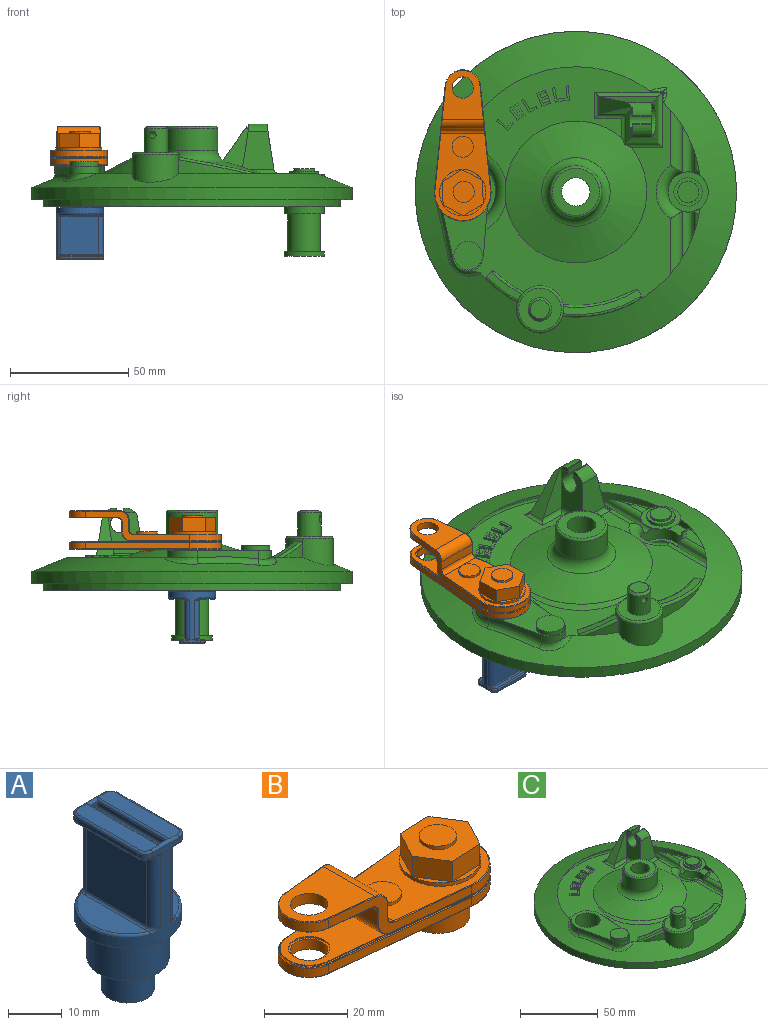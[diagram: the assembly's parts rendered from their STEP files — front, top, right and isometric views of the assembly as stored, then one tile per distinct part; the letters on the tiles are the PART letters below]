
ASSEMBLY  parts=3 mates=2
PART A: 97 faces, bbox 21.6x22x38 mm
  f0: plane 19x3.5mm, normal (0,0,1), area 65.5mm2, adj f39,f40,f42,f59,f60,f61
  f1: plane 19x3.5mm, normal (0,0,1), area 65.5mm2, adj f39,f41,f42,f56,f57,f58
  f2: cylinder r=10mm len=20mm, axis (0,0,-1), area 247.8mm2, adj f5,f23,f24,f25,f26,f27,f28,f30
  f3: plane 16x15.87mm, normal (1,0,0), area 254mm2, adj f25,f26,f31,f76
  f4: plane 16x15.87mm, normal (-1,0,0), area 254mm2, adj f23,f24,f37,f87
  f5: plane 20x20mm, normal (0,0,-1), area 127.9mm2, adj f2,f93
  f6: plane 17.81x6.2mm, normal (0,0,1), area 76.9mm2, adj f34,f35,f37,f38
  f7: plane 17.81x6.2mm, normal (0,0,1), area 76.9mm2, adj f28,f29,f31,f32
  f8: plane 7x1.5mm, normal (0,1,0), area 8.1mm2, adj f19,f22,f39,f47,f49,f51,f67,f69
  f9: plane 16x1mm, normal (-1,0,0), area 16mm2, adj f19,f20,f60,f66
  f10: plane 7x1.5mm, normal (0,-1,0), area 8.1mm2, adj f20,f21,f42,f48,f50,f52,f62,f63
  f11: plane 19x2.05mm, normal (0,0,-1), area 28.1mm2, adj f64,f65,f66,f68,f70,f86,f87,f88
  f12: plane 16x1mm, normal (1,0,0), area 16mm2, adj f21,f22,f55,f57
  f13: plane 19x2.05mm, normal (0,0,-1), area 28.1mm2, adj f51,f52,f53,f54,f55,f75,f76,f77
  f14: plane 2x1mm, normal (0,-1,0), area 2mm2, adj f15,f17,f39,f43
  f15: plane 18x1mm, normal (1,0,0), area 18mm2, adj f14,f16,f40,f44
  f16: plane 2x1mm, normal (0,1,0), area 2mm2, adj f15,f17,f42,f46
  f17: plane 18x1mm, normal (-1,0,0), area 18mm2, adj f14,f16,f41,f45
  f18: plane 17x1mm, normal (0,0,1), area 17mm2, adj f43,f44,f45,f46
  f19: cylinder r=2mm len=2mm, axis (0,0,-1), area 3.1mm2, adj f8,f9,f61,f68
  f20: cylinder r=2mm len=2mm, axis (0,0,1), area 3.1mm2, adj f9,f10,f59,f65
  f21: cylinder r=2mm len=2mm, axis (0,0,-1), area 3.1mm2, adj f10,f12,f54,f56
  f22: cylinder r=2mm len=2mm, axis (0,0,1), area 3.1mm2, adj f8,f12,f53,f58
  f23: cylinder r=2mm len=16.38mm, axis (0,0,-1), area 46.6mm2, adj f2,f4,f35,f88,f89,f90
  f24: cylinder r=2mm len=16.38mm, axis (0,0,-1), area 46.6mm2, adj f2,f4,f38,f84,f85,f86
  f25: cylinder r=2mm len=16.38mm, axis (0,0,-1), area 46.6mm2, adj f2,f3,f29,f73,f74,f75
  f26: cylinder r=2mm len=16.38mm, axis (0,0,-1), area 46.6mm2, adj f2,f3,f32,f77,f78,f79
  f27: bspline ~2.56x1.18mm, area 0.6mm2, adj f2,f28,f29
  f28: torus R=9.5mm, axis (0,0,1), area 18.7mm2, adj f2,f7,f27,f30
  f29: torus R=2.5mm, axis (0,0,1), area 1.5mm2, adj f7,f25,f27,f31
  f30: bspline ~2.56x1.18mm, area 0.6mm2, adj f2,f28,f32
  f31: cylinder r=0.5mm len=15.87mm, axis (0,1,0), area 12.5mm2, adj f3,f7,f29,f32
  f32: torus R=2.5mm, axis (0,0,1), area 1.5mm2, adj f7,f26,f30,f31
  f33: bspline ~2.56x1.18mm, area 0.6mm2, adj f2,f34,f35
  f34: torus R=9.5mm, axis (0,0,1), area 18.7mm2, adj f2,f6,f33,f36
  f35: torus R=2.5mm, axis (0,0,1), area 1.5mm2, adj f6,f23,f33,f37
  f36: bspline ~2.56x1.18mm, area 0.6mm2, adj f2,f34,f38
  f37: cylinder r=0.5mm len=15.87mm, axis (0,-1,0), area 12.5mm2, adj f4,f6,f35,f38
  f38: torus R=2.5mm, axis (0,0,1), area 1.5mm2, adj f6,f24,f36,f37
  f39: cylinder r=0.5mm len=7mm, axis (1,0,0), area 7.5mm2, adj f0,f1,f8,f14,f40,f41,f58,f61
  f40: cylinder r=0.5mm len=19mm, axis (0,1,0), area 14.5mm2, adj f0,f15,f39,f42
  f41: cylinder r=0.5mm len=19mm, axis (0,-1,0), area 14.5mm2, adj f1,f17,f39,f42
  f42: cylinder r=0.5mm len=7mm, axis (-1,0,0), area 7.5mm2, adj f0,f1,f10,f16,f40,f41,f56,f59
  f43: cylinder r=0.5mm len=2mm, axis (-1,0,0), area 1.2mm2, adj f14,f18,f44,f45
  f44: cylinder r=0.5mm len=18mm, axis (0,-1,0), area 13.7mm2, adj f15,f18,f43,f46
  f45: cylinder r=0.5mm len=18mm, axis (0,1,0), area 13.7mm2, adj f17,f18,f43,f46
  f46: cylinder r=0.5mm len=2mm, axis (1,0,0), area 1.2mm2, adj f16,f18,f44,f45
  f47: bspline ~1.52x0.32mm, area 0.1mm2, adj f8,f49,f81
  f48: bspline ~1.52x0.32mm, area 0.1mm2, adj f10,f50,f71
  f49: bspline ~1.38x0.57mm, area 0.3mm2, adj f8,f47,f51,f79,f80
  f50: bspline ~1.38x0.57mm, area 0.3mm2, adj f10,f48,f52,f72,f73
  f51: cylinder r=0.5mm len=1.25mm, axis (1,0,0), area 0.9mm2, adj f8,f13,f49,f53,f78
  f52: cylinder r=0.5mm len=1.25mm, axis (-1,0,0), area 0.9mm2, adj f10,f13,f50,f54,f74
  f53: torus R=1.5mm, axis (0,0,1), area 2.2mm2, adj f13,f22,f51,f55
  f54: torus R=1.5mm, axis (0,0,1), area 2.2mm2, adj f13,f21,f52,f55
  f55: cylinder r=0.5mm len=16mm, axis (0,-1,0), area 12.6mm2, adj f12,f13,f53,f54
  f56: torus R=1.5mm, axis (0,0,1), area 2.2mm2, adj f1,f21,f42,f57
  f57: cylinder r=0.5mm len=16mm, axis (0,1,0), area 12.6mm2, adj f1,f12,f56,f58
  f58: torus R=1.5mm, axis (0,0,1), area 2.2mm2, adj f1,f22,f39,f57
  f59: torus R=1.5mm, axis (0,0,1), area 2.2mm2, adj f0,f20,f42,f60
  f60: cylinder r=0.5mm len=16mm, axis (0,-1,0), area 12.6mm2, adj f0,f9,f59,f61
  f61: torus R=1.5mm, axis (0,0,1), area 2.2mm2, adj f0,f19,f39,f60
  f62: bspline ~1.52x0.32mm, area 0.1mm2, adj f10,f63,f82
  f63: bspline ~1.38x0.57mm, area 0.3mm2, adj f10,f62,f64,f83,f84
  f64: cylinder r=0.5mm len=1.25mm, axis (-1,0,0), area 0.9mm2, adj f10,f11,f63,f65,f85
  f65: torus R=1.5mm, axis (0,0,1), area 2.2mm2, adj f11,f20,f64,f66
  f66: cylinder r=0.5mm len=16mm, axis (0,1,0), area 12.6mm2, adj f9,f11,f65,f68
  f67: bspline ~1.52x0.32mm, area 0.1mm2, adj f8,f69,f92
  f68: torus R=1.5mm, axis (0,0,1), area 2.2mm2, adj f11,f19,f66,f70
  f69: bspline ~1.38x0.57mm, area 0.3mm2, adj f8,f67,f70,f90,f91
  f70: cylinder r=0.5mm len=1.25mm, axis (1,0,0), area 0.9mm2, adj f8,f11,f68,f69,f89
  f71: bspline ~1.6x0.24mm, area 0.1mm2, adj f2,f48,f72
  f72: bspline ~0.49x0.24mm, area 0mm2, adj f2,f50,f71,f73
  f73: bspline ~1.27x0.43mm, area 0.3mm2, adj f25,f50,f72,f74
  f74: bspline ~1.32x0.85mm, area 0.5mm2, adj f25,f52,f73,f75
  f75: torus R=2.5mm, axis (0,0,1), area 1.2mm2, adj f13,f25,f74,f76
  f76: cylinder r=0.5mm len=15.87mm, axis (0,-1,0), area 12.5mm2, adj f3,f13,f75,f77
  f77: torus R=2.5mm, axis (0,0,1), area 1.2mm2, adj f13,f26,f76,f78
  f78: bspline ~1.32x0.85mm, area 0.5mm2, adj f26,f51,f77,f79
  f79: bspline ~1.27x0.43mm, area 0.3mm2, adj f26,f49,f78,f80
  f80: bspline ~0.5x0.24mm, area 0mm2, adj f2,f49,f79,f81
  f81: bspline ~1.93x0.29mm, area 0.1mm2, adj f2,f47,f80
  f82: bspline ~1.93x0.29mm, area 0.1mm2, adj f2,f62,f83
  f83: bspline ~0.5x0.24mm, area 0mm2, adj f2,f63,f82,f84
  f84: bspline ~1.27x0.43mm, area 0.3mm2, adj f24,f63,f83,f85
  f85: bspline ~1.32x0.85mm, area 0.5mm2, adj f24,f64,f84,f86
  f86: torus R=2.5mm, axis (0,0,1), area 1.2mm2, adj f11,f24,f85,f87
  f87: cylinder r=0.5mm len=15.87mm, axis (0,1,0), area 12.5mm2, adj f4,f11,f86,f88
  f88: torus R=2.5mm, axis (0,0,1), area 1.2mm2, adj f11,f23,f87,f89
  f89: bspline ~1.32x0.85mm, area 0.5mm2, adj f23,f70,f88,f90
  f90: bspline ~1.27x0.43mm, area 0.3mm2, adj f23,f69,f89,f91
  f91: bspline ~0.49x0.24mm, area 0mm2, adj f2,f69,f90,f92
  f92: bspline ~1.6x0.24mm, area 0.1mm2, adj f2,f67,f91
  f93: cylinder r=7.7mm len=15.4mm, axis (0,0,1), area 435.4mm2, adj f5,f94
  f94: plane 15.4x15.4mm, normal (0,0,-1), area 107.7mm2, adj f93,f95
  f95: cylinder r=5mm len=10mm, axis (0,0,1), area 219.9mm2, adj f94,f96
  f96: plane 10x10mm, normal (0,0,-1), area 78.5mm2, adj f95
PART B: 91 faces, bbox 65.6x26x25.4 mm
  f0: plane 36.8x23.6mm, normal (0,0,1), area 381.9mm2, adj f28,f55,f56,f57,f67,f69
  f1: plane 17.66x4.03mm, normal (-1,0,0), area 71.1mm2, adj f25,f27,f48,f49
  f2: plane 18.28x0.31mm, normal (-1,0,0), area 1.8mm2, adj f12,f14,f15,f16,f25,f29,f32,f42
  f3: plane 10x10mm, normal (0,0,1), area 14.9mm2, adj f7,f13
  f4: cylinder r=7.5mm len=14.92mm, axis (0,0,-1), area 57.3mm2, adj f5,f8,f34,f38
  f5: plane 44.05x4.48mm, normal (-0.1,-0.99,0), area 115.1mm2, adj f4,f6,f33,f37
  f6: cylinder r=12mm len=24mm, axis (0,0,-1), area 104.3mm2, adj f5,f8,f35,f39
  f7: cylinder r=4.5mm len=9mm, axis (0,0,-1), area 84.8mm2, adj f3,f10
  f8: plane 44.05x4.48mm, normal (-0.1,0.99,0), area 115.1mm2, adj f4,f6,f36,f40
  f9: plane 63.6x23.6mm, normal (0,0,1), area 14.9mm2, adj f29,f30,f31,f32,f37,f38,f39,f40
  f10: plane 63.6x23.6mm, normal (0,0,-1), area 875.7mm2, adj f7,f33,f34,f35,f36,f86,f87
  f11: cylinder r=7mm len=13.93mm, axis (0,0,-1), area 4.1mm2, adj f12,f14,f15,f30
  f12: plane 18.21x1.85mm, normal (-0.1,-0.99,0), area 3.7mm2, adj f2,f11,f15,f29
  f13: cylinder r=5mm len=10mm, axis (0,0,-1), area 12.6mm2, adj f3,f15
  f14: plane 18.21x1.85mm, normal (-0.1,0.99,0), area 3.7mm2, adj f2,f11,f15,f32
  f15: plane 24.5x17.63mm, normal (0,0,1), area 275.8mm2, adj f2,f11,f12,f13,f14
  f16: plane 38.8x23.6mm, normal (0,0,-1), area 9.1mm2, adj f2,f29,f31,f32,f41,f42,f43
  f17: plane 44.05x12.6mm, normal (-0.1,0.99,0), area 137.2mm2, adj f19,f22,f42,f44,f46,f48,f50,f52
  f18: plane 44.05x12.6mm, normal (-0.1,-0.99,0), area 137.2mm2, adj f19,f22,f43,f45,f47,f49,f51,f53
  f19: cylinder r=12mm len=24mm, axis (0,0,-1), area 104.3mm2, adj f17,f18,f41,f55
  f20: plane 18.19x4mm, normal (1,0,0), area 72.8mm2, adj f26,f28,f60,f61
  f21: plane 20.8x17.42mm, normal (0,0,1), area 236.7mm2, adj f23,f26,f64,f65,f66
  f22: cylinder r=7.5mm len=14.92mm, axis (0,0,1), area 57.3mm2, adj f17,f18,f54,f66
  f23: cylinder r=4.5mm len=9mm, axis (0,0,1), area 84.8mm2, adj f21,f24
  f24: plane 19.8x17.22mm, normal (0,0,-1), area 219.4mm2, adj f23,f27,f52,f53,f54
  f25: cylinder r=4mm len=18.24mm, axis (0,1,0), area 94.7mm2, adj f1,f2,f46,f47
  f26: cylinder r=4mm len=18.19mm, axis (0,-1,0), area 111.9mm2, adj f20,f21,f62,f63
  f27: cylinder r=2mm len=17.66mm, axis (0,1,0), area 54.8mm2, adj f1,f24,f50,f51
  f28: cylinder r=2mm len=18.64mm, axis (0,1,0), area 57.9mm2, adj f0,f20,f58,f59
  f29: cylinder r=0.2mm len=44.07mm, axis (0.99,-0.1,0), area 22.1mm2, adj f2,f9,f12,f16,f30,f31
  f30: torus R=7.2mm, axis (0,0,1), area 6.5mm2, adj f9,f11,f29,f32
  f31: torus R=11.7mm, axis (0,0,1), area 24.3mm2, adj f9,f16,f29,f32
  f32: cylinder r=0.2mm len=44.07mm, axis (-0.99,-0.1,0), area 22.1mm2, adj f2,f9,f14,f16,f30,f31
  f33: cylinder r=0.2mm len=44.07mm, axis (0.99,-0.1,0), area 13.9mm2, adj f5,f10,f34,f35
  f34: torus R=7.3mm, axis (0,0,1), area 6.9mm2, adj f4,f10,f33,f36
  f35: torus R=11.8mm, axis (0,0,1), area 12.5mm2, adj f6,f10,f33,f36
  f36: cylinder r=0.2mm len=44.07mm, axis (-0.99,-0.1,0), area 13.9mm2, adj f8,f10,f34,f35
  f37: cylinder r=0.2mm len=44.07mm, axis (-0.99,0.1,0), area 13.9mm2, adj f5,f9,f38,f39
  f38: torus R=7.3mm, axis (0,0,1), area 6.9mm2, adj f4,f9,f37,f40
  f39: torus R=11.8mm, axis (0,0,1), area 12.5mm2, adj f6,f9,f37,f40
  f40: cylinder r=0.2mm len=44.07mm, axis (0.99,0.1,0), area 13.9mm2, adj f8,f9,f38,f39
  f41: torus R=11.8mm, axis (0,0,1), area 12.5mm2, adj f16,f19,f42,f43
  f42: cylinder r=0.2mm len=25.83mm, axis (-0.99,-0.1,0), area 8.1mm2, adj f2,f16,f17,f41,f44
  f43: cylinder r=0.2mm len=25.83mm, axis (0.99,-0.1,0), area 8.1mm2, adj f2,f16,f18,f41,f45
  f44: cylinder r=0.2mm len=0.26mm, axis (0,0,1), area 0mm2, adj f2,f17,f42,f46
  f45: cylinder r=0.2mm len=0.26mm, axis (0,0,1), area 0mm2, adj f2,f18,f43,f47
  f46: bspline ~3.91x3.18mm, area 1.6mm2, adj f2,f17,f25,f44,f48
  f47: bspline ~3.91x3.18mm, area 1.6mm2, adj f2,f18,f25,f45,f49
  f48: cylinder r=0.2mm len=4.03mm, axis (0,0,1), area 1.2mm2, adj f1,f17,f46,f50
  f49: cylinder r=0.2mm len=4.03mm, axis (0,0,1), area 1.2mm2, adj f1,f18,f47,f51
  f50: bspline ~2.58x2.2mm, area 1mm2, adj f17,f27,f48,f52
  f51: bspline ~2.58x2.58mm, area 1mm2, adj f18,f27,f49,f53
  f52: cylinder r=0.2mm len=13.26mm, axis (-0.99,-0.1,0), area 4.2mm2, adj f17,f24,f50,f54
  f53: cylinder r=0.2mm len=13.26mm, axis (-0.99,0.1,0), area 4.2mm2, adj f18,f24,f51,f54
  f54: torus R=7.3mm, axis (0,0,1), area 6.9mm2, adj f22,f24,f52,f53
  f55: torus R=11.8mm, axis (0,0,1), area 12.5mm2, adj f0,f19,f56,f57
  f56: cylinder r=0.2mm len=23.83mm, axis (0.99,0.1,0), area 7.5mm2, adj f0,f17,f55,f58
  f57: cylinder r=0.2mm len=23.83mm, axis (-0.99,0.1,0), area 7.5mm2, adj f0,f18,f55,f59
  f58: bspline ~2.22x2.2mm, area 1.1mm2, adj f17,f28,f56,f60
  f59: bspline ~2.22x2.2mm, area 1.1mm2, adj f18,f28,f57,f61
  f60: cylinder r=0.2mm len=4mm, axis (0,0,-1), area 1.3mm2, adj f17,f20,f58,f62
  f61: cylinder r=0.2mm len=4mm, axis (0,0,-1), area 1.3mm2, adj f18,f20,f59,f63
  f62: bspline ~4.02x4mm, area 2mm2, adj f17,f26,f60,f64
  f63: bspline ~4.02x4mm, area 2mm2, adj f18,f26,f61,f65
  f64: cylinder r=0.2mm len=14.26mm, axis (0.99,0.1,0), area 4.5mm2, adj f17,f21,f62,f66
  f65: cylinder r=0.2mm len=14.26mm, axis (0.99,-0.1,0), area 4.5mm2, adj f18,f21,f63,f66
  f66: torus R=7.3mm, axis (0,0,1), area 6.9mm2, adj f21,f22,f64,f65
  f67: cylinder r=4.5mm len=9mm, axis (0,0,-1), area 28.3mm2, adj f0,f68
  f68: plane 9x9mm, normal (0,0,1), area 63.6mm2, adj f67
  f69: cylinder r=9.81mm len=19.63mm, axis (0,0,-1), area 61.7mm2, adj f0,f70,f71,f72,f73,f74,f75
  f70: plane 8.3x5.24mm, normal (0,0,1), area 8.7mm2, adj f69,f82
  f71: plane 9.81x1.52mm, normal (0,0,1), area 8.7mm2, adj f69,f81
  f72: plane 8.69x4.57mm, normal (0,0,1), area 8.7mm2, adj f69,f80
  f73: plane 8.3x5.24mm, normal (0,0,1), area 8.7mm2, adj f69,f79
  f74: plane 9.81x1.52mm, normal (0,0,1), area 8.7mm2, adj f69,f78
  f75: plane 8.69x4.57mm, normal (0,0,1), area 8.7mm2, adj f69,f77
  f76: plane 19.61x17.38mm, normal (0,0,1), area 186.7mm2, adj f77,f78,f79,f80,f81,f82,f83
  f77: plane 8.69x6mm, normal (-0.89,0.46,0), area 58.9mm2, adj f75,f76,f78,f82
  f78: plane 9.81x6mm, normal (-0.04,1,0), area 58.9mm2, adj f74,f76,f77,f79
  f79: plane 8.3x6mm, normal (0.85,0.53,0), area 58.9mm2, adj f73,f76,f78,f80
  f80: plane 8.69x6mm, normal (0.89,-0.46,0), area 58.9mm2, adj f72,f76,f79,f81
  f81: plane 9.81x6mm, normal (0.04,-1,0), area 58.9mm2, adj f71,f76,f80,f82
  f82: plane 8.3x6mm, normal (-0.85,-0.53,0), area 58.9mm2, adj f70,f76,f77,f81
  f83: cylinder r=4.5mm len=9mm, axis (0,0,-1), area 28.3mm2, adj f76,f84
  f84: plane 9x9mm, normal (0,0,1), area 63.6mm2, adj f83
  f85: plane 0.3x0.3mm, normal (0,0,-1), area 0.1mm2, adj f86
  f86: torus R=0.15mm, axis (0,0,1), area 34.4mm2, adj f10,f85
  f87: cylinder r=7.7mm len=15.4mm, axis (0,0,1), area 435.4mm2, adj f10,f88
  f88: plane 15.4x15.4mm, normal (0,0,-1), area 99.7mm2, adj f87,f89
  f89: cylinder r=5.25mm len=10.5mm, axis (0,0,-1), area 263.9mm2, adj f88,f90
  f90: plane 10.5x10.5mm, normal (0,0,-1), area 86.6mm2, adj f89
PART C: 208 faces, bbox 138.4x138.4x58.4 mm
  f0: plane 112.54x103.07mm, normal (0,0,1), area 4306.9mm2, adj f3,f93,f94,f95,f99,f101,f103,f111
  f1: plane 3.88x2mm, normal (-1,0,0), area 6.6mm2, adj f5,f130,f133,f135,f142
  f2: plane 4.97x2mm, normal (1,0,0), area 3.1mm2, adj f131,f134,f136,f137,f140
  f3: cone r=53mm half-angle=68.2deg, axis (0,0,-1), area 5588.4mm2, adj f0,f21,f99,f100,f101,f102,f103,f113
  f4: cylinder r=4mm len=8.03mm, axis (1,0,0), area 177mm2, adj f135,f136,f138,f142
  f5: plane 8x0.5mm, normal (0,0,1), area 4mm2, adj f1,f7,f133,f135
  f6: plane 4.97x2mm, normal (-1,0,0), area 7.2mm2, adj f131,f134,f136,f142
  f7: plane 4.97x2mm, normal (1,0,0), area 3.1mm2, adj f5,f133,f135,f137,f140
  f8: cylinder r=3mm len=6mm, axis (0,0,-1), area 30.3mm2, adj f9,f10,f11,f63,f82,f83,f84,f85
  f9: plane 1.69x1.69mm, normal (0,0,-1), area 1.8mm2, adj f8,f85,f91
  f10: plane 1.69x1.69mm, normal (0,0,-1), area 1.8mm2, adj f8,f88,f89
  f11: plane 1.69x1.69mm, normal (0,0,-1), area 1.8mm2, adj f8,f86,f87
  f12: cylinder r=61mm len=122mm, axis (0,0,-1), area 1352mm2, adj f17,f33,f38,f39,f44,f46,f51,f53
  f13: plane 112.27x96.16mm, normal (0,0,-1), area 5588.8mm2, adj f24,f60,f62,f65,f66,f68,f69,f70
  f14: cylinder r=8.5mm len=17mm, axis (0,0,1), area 334.5mm2, adj f27,f33,f38,f39,f40,f42,f47,f49
  f15: cylinder r=7mm len=16mm, axis (0,0,1), area 703.7mm2, adj f27,f29
  f16: cylinder r=66mm len=132mm, axis (0,0,-1), area 1451.4mm2, adj f19,f20
  f17: plane 126x126mm, normal (0,0,-1), area 1175.7mm2, adj f12,f18,f54,f55,f56,f57,f58,f59
  f18: cylinder r=63mm len=126mm, axis (0,0,-1), area 2573mm2, adj f17,f19
  f19: plane 132x132mm, normal (0,0,-1), area 1215.8mm2, adj f16,f18
  f20: plane 136x136mm, normal (0,0,-1), area 841.9mm2, adj f16,f21
  f21: cylinder r=68mm len=136mm, axis (0,0,-1), area 2136.3mm2, adj f3,f20
  f22: plane 31x31mm, normal (0,0,-1), area 47.9mm2, adj f24,f25
  f23: plane 21x21mm, normal (0,0,-1), area 233.3mm2, adj f25,f26
  f24: cone r=15.5mm half-angle=76deg, axis (0,0,-1), area 1671mm2, adj f13,f22
  f25: cone r=10.5mm half-angle=56.3deg, axis (0,0,1), area 433.3mm2, adj f22,f23
  f26: cylinder r=6mm len=25mm, axis (0,0,-1), area 942.5mm2, adj f23,f110
  f27: plane 17x17mm, normal (0,0,-1), area 73mm2, adj f14,f15
  f28: cylinder r=8.5mm len=17mm, axis (0,0,1), area 106.8mm2, adj f29,f30
  f29: plane 17x17mm, normal (0,0,1), area 73mm2, adj f15,f28
  f30: plane 17x17mm, normal (0,0,-1), area 227mm2, adj f28
  f31: plane 2.09x1.5mm, normal (0,-1,0), area 3.1mm2, adj f33,f36,f40,f46
  f32: plane 2.09x1.5mm, normal (0,1,0), area 3.1mm2, adj f33,f37,f47,f53
  f33: plane 14.6x6.94mm, normal (0,0,-1), area 52.1mm2, adj f12,f14,f31,f32,f40,f46,f47,f53
  f34: plane 19.01x5.68mm, normal (0,0,-1), area 59.4mm2, adj f36,f42,f43,f44
  f35: plane 19.01x5.68mm, normal (0,0,-1), area 59.4mm2, adj f37,f49,f50,f51
  f36: cylinder r=2.5mm len=2.5mm, axis (-1,0,0), area 8.2mm2, adj f31,f34,f41,f45
  f37: cylinder r=2.5mm len=2.5mm, axis (1,0,0), area 8.2mm2, adj f32,f35,f48,f52
  f38: cylinder r=2.5mm len=33.02mm, axis (0,-1,0), area 215.6mm2, adj f12,f14,f42,f43,f44,f66,f68,f70
  f39: cylinder r=2.5mm len=33.02mm, axis (0,1,0), area 215.6mm2, adj f12,f14,f49,f50,f51,f70,f71,f73
  f40: cylinder r=2.5mm len=1.93mm, axis (0,0,1), area 3.3mm2, adj f14,f31,f33,f41
  f41: sphere r=2.5mm, area 6.6mm2, adj f36,f40,f42
  f42: torus R=11mm, axis (0,0,-1), area 18.9mm2, adj f14,f34,f38,f41,f43
  f43: cylinder r=2.5mm len=26.73mm, axis (0,-1,0), area 73.4mm2, adj f34,f38,f42,f44
  f44: torus R=58.5mm, axis (0,0,-1), area 104.3mm2, adj f12,f34,f38,f43,f45
  f45: sphere r=2.5mm, area 14mm2, adj f36,f44,f46
  f46: cylinder r=2.5mm len=2.8mm, axis (0,0,-1), area 6.3mm2, adj f12,f31,f33,f45
  f47: cylinder r=2.5mm len=1.93mm, axis (0,0,1), area 3.3mm2, adj f14,f32,f33,f48
  f48: sphere r=2.5mm, area 6.6mm2, adj f37,f47,f49
  f49: torus R=11mm, axis (0,0,-1), area 18.9mm2, adj f14,f35,f39,f48,f50
  f50: cylinder r=2.5mm len=26.73mm, axis (0,1,0), area 73.4mm2, adj f35,f39,f49,f51
  f51: torus R=58.5mm, axis (0,0,-1), area 104.3mm2, adj f12,f35,f39,f50,f52
  f52: sphere r=2.5mm, area 12.9mm2, adj f37,f51,f53
  f53: cylinder r=2.5mm len=2.8mm, axis (0,0,-1), area 6.3mm2, adj f12,f32,f33,f52
  f54: cylinder r=13.5mm len=27mm, axis (0,0,1), area 245mm2, adj f17,f58,f59,f72,f77,f78
  f55: cylinder r=8mm len=17mm, axis (0,0,1), area 854.5mm2, adj f17,f96
  f56: cylinder r=3mm len=4mm, axis (0,0,1), area 10.1mm2, adj f12,f17,f58,f75
  f57: cylinder r=3mm len=4mm, axis (0,0,1), area 10.1mm2, adj f12,f17,f59,f80
  f58: cylinder r=2mm len=4mm, axis (0,0,1), area 13.1mm2, adj f17,f54,f56,f76
  f59: cylinder r=2mm len=4mm, axis (0,0,1), area 13.1mm2, adj f17,f54,f57,f79
  f60: cylinder r=5mm len=10mm, axis (0,0,-1), area 31.4mm2, adj f13,f61,f64
  f61: plane 10x10mm, normal (0,0,-1), area 78.5mm2, adj f60
  f62: cylinder r=5.5mm len=11mm, axis (0,0,-1), area 34.6mm2, adj f13,f63,f67
  f63: plane 11x11mm, normal (0,0,-1), area 66.8mm2, adj f8,f62
  f64: bspline ~8.08x6.88mm, area 47.4mm2, adj f12,f60,f65,f66
  f65: torus R=56mm, axis (0,0,-1), area 298.6mm2, adj f12,f13,f64,f67
  f66: torus R=56mm, axis (0,0,-1), area 492.6mm2, adj f12,f13,f38,f64,f68
  f67: bspline ~11.58x9.29mm, area 61.8mm2, adj f12,f62,f65,f69
  f68: cylinder r=5mm len=33.02mm, axis (0,-1,0), area 229.2mm2, adj f13,f38,f66,f70
  f69: torus R=56mm, axis (0,0,-1), area 9.1mm2, adj f12,f13,f67,f74
  f70: torus R=13.5mm, axis (0,0,-1), area 184.6mm2, adj f13,f14,f38,f39,f68,f71
  f71: cylinder r=5mm len=33.02mm, axis (0,1,0), area 229.2mm2, adj f13,f39,f70,f73
  f72: torus R=18.5mm, axis (0,0,-1), area 411.1mm2, adj f13,f54,f77,f78
  f73: torus R=56mm, axis (0,0,-1), area 935.2mm2, adj f12,f13,f39,f71,f81
  f74: bspline ~9.35x7.51mm, area 56.8mm2, adj f12,f13,f69,f75
  f75: bspline ~5.44x5mm, area 16mm2, adj f13,f56,f74,f76
  f76: bspline ~5.42x5mm, area 20.6mm2, adj f13,f58,f75,f77
  f77: bspline ~7.98x6.82mm, area 42.9mm2, adj f13,f54,f72,f76
  f78: bspline ~7.98x6.82mm, area 42.9mm2, adj f13,f54,f72,f79
  f79: bspline ~5.42x5mm, area 20.6mm2, adj f13,f59,f78,f80
  f80: bspline ~5.44x5mm, area 16mm2, adj f13,f57,f79,f81
  f81: bspline ~9.35x7.51mm, area 56.8mm2, adj f12,f13,f73,f80
  f82: plane 1.69x1.69mm, normal (0,0,-1), area 1.8mm2, adj f8,f84,f90
  f83: plane 6x6mm, normal (0,0,-1), area 2.4mm2, adj f8,f84,f85,f86,f87,f88,f89,f90
  f84: plane 2.93x1.53mm, normal (0.83,0,-0.55), area 4.2mm2, adj f8,f82,f83,f90
  f85: plane 2.93x1.53mm, normal (0,-0.83,-0.55), area 4.2mm2, adj f8,f9,f83,f91
  f86: plane 2.93x1.53mm, normal (0,-0.83,-0.55), area 4.2mm2, adj f8,f11,f83,f87
  f87: plane 2.93x1.53mm, normal (0.83,0,-0.55), area 4.2mm2, adj f8,f11,f83,f86
  f88: plane 2.93x1.53mm, normal (0,0.83,-0.55), area 4.2mm2, adj f8,f10,f83,f89
  f89: plane 2.93x1.53mm, normal (-0.83,0,-0.55), area 4.2mm2, adj f8,f10,f83,f88
  f90: plane 2.93x1.53mm, normal (0,0.83,-0.55), area 4.2mm2, adj f8,f82,f83,f84
  f91: plane 2.93x1.53mm, normal (-0.83,0,-0.55), area 4.2mm2, adj f8,f9,f83,f85
  f92: plane 26.09x5.77mm, normal (-0.98,-0.22,0), area 75.2mm2, adj f93,f95,f96,f100
  f93: cylinder r=6.5mm len=12.83mm, axis (0,0,-1), area 56.9mm2, adj f0,f92,f94,f96,f99
  f94: plane 26.62x3mm, normal (1,-0.08,0), area 80.1mm2, adj f0,f93,f95,f96
  f95: cylinder r=10.5mm len=21mm, axis (0,0,-1), area 108.2mm2, adj f0,f92,f94,f96,f101
  f96: plane 43.94x21mm, normal (0,0,1), area 389.4mm2, adj f55,f92,f93,f94,f95,f97
  f97: cylinder r=6mm len=12mm, axis (0,0,-1), area 75.4mm2, adj f96,f98
  f98: plane 12x12mm, normal (0,0,1), area 113.1mm2, adj f97
  f99: bspline ~14.97x8.59mm, area 40.7mm2, adj f0,f3,f93,f100
  f100: bspline ~57.18x14.42mm, area 91.7mm2, adj f3,f92,f99,f101
  f101: bspline ~16.88x10.21mm, area 37mm2, adj f0,f3,f95,f100
  f102: cylinder r=8.5mm len=12.24mm, axis (0,0,1), area 0mm2, adj f3,f105
  f103: cylinder r=8.5mm len=17mm, axis (0,0,1), area 11.6mm2, adj f0,f3,f105
  f104: cylinder r=6mm len=12mm, axis (0,0,1), area 49mm2, adj f105,f106
  f105: plane 17x17mm, normal (0,0,1), area 113.9mm2, adj f102,f103,f104
  f106: plane 12x12mm, normal (0,0,1), area 49.5mm2, adj f104,f108
  f107: plane 9x9mm, normal (0,0,1), area 63.6mm2, adj f108
  f108: cylinder r=4.5mm len=9mm, axis (0,0,-1), area 28.3mm2, adj f106,f107
  f109: cylinder r=11mm len=22mm, axis (0,0,-1), area 645.2mm2, adj f112,f207
  f110: plane 20x20mm, normal (0,0,1), area 201.1mm2, adj f26,f207
  f111: cone r=11mm half-angle=72.5deg, axis (0,0,-1), area 2268.7mm2, adj f0,f112,f144,f146
  f112: torus R=16mm, axis (0,0,1), area 486mm2, adj f109,f111
  f113: cylinder r=10mm len=20mm, axis (0,0,1), area 509.6mm2, adj f0,f3,f118,f119,f120,f121,f122,f123
  f114: plane 18x18mm, normal (0,0,1), area 175.9mm2, adj f117,f128
  f115: plane 8x8mm, normal (0,0,1), area 50.3mm2, adj f129
  f116: cylinder r=1.5mm len=10mm, axis (-0.29,-0.96,0), area 89.9mm2, adj f117
  f117: cylinder r=5mm len=10mm, axis (0,0,-1), area 307mm2, adj f114,f116,f129
  f118: cylinder r=48mm len=10.97mm, axis (0,0,-1), area 38.1mm2, adj f0,f113,f124
  f119: cylinder r=53mm len=11.81mm, axis (0,0,-1), area 42.6mm2, adj f3,f113,f125
  f120: cylinder r=53mm len=29.61mm, axis (0,0,-1), area 90mm2, adj f3,f113,f127
  f121: cylinder r=48mm len=26.97mm, axis (0,0,-1), area 77.4mm2, adj f0,f113,f126
  f122: plane 33.1x10.48mm, normal (0.18,0.1,0.98), area 103.2mm2, adj f0,f113,f126,f127
  f123: plane 15.04x12.32mm, normal (-0.28,0.26,0.92), area 53.3mm2, adj f0,f113,f124,f125
  f124: bspline ~13.68x10.17mm, area 25.1mm2, adj f0,f113,f118,f123
  f125: bspline ~26.12x19.53mm, area 27.6mm2, adj f0,f113,f119,f123
  f126: bspline ~31.65x8.21mm, area 46.5mm2, adj f0,f113,f121,f122
  f127: bspline ~43.46x13.25mm, area 54.5mm2, adj f0,f113,f120,f122
  f128: torus R=9mm, axis (0,0,1), area 95.1mm2, adj f113,f114
  f129: cone r=4mm half-angle=45deg, axis (0,0,-1), area 40mm2, adj f115,f117
  f130: plane 1.43x0.96mm, normal (0,-1,0), area 1mm2, adj f1,f132,f133,f143
  f131: plane 8x0.5mm, normal (0,0,1), area 4mm2, adj f2,f6,f134,f136
  f132: plane 19.3x13.84mm, normal (-0.81,0,0.58), area 103.1mm2, adj f130,f133,f139,f143,f145,f147,f149
  f133: cylinder r=6mm len=10.59mm, axis (1,0,0), area 58.3mm2, adj f1,f5,f7,f130,f132,f139,f140
  f134: cylinder r=6mm len=8.42mm, axis (-1,0,0), area 53.6mm2, adj f2,f6,f131,f140,f141,f142
  f135: plane 8.13x2.79mm, normal (0,-1,0), area 22.1mm2, adj f1,f4,f5,f7,f137,f138,f142
  f136: plane 8.13x2.79mm, normal (0,1,0), area 22.1mm2, adj f2,f4,f6,f131,f137,f138,f142
  f137: cylinder r=6.65mm len=13.3mm, axis (1,0,0), area 36mm2, adj f2,f7,f135,f136,f138,f140
  f138: plane 13.3x13.13mm, normal (1,0,0), area 80.6mm2, adj f4,f135,f136,f137
  f139: plane 24.52x15.97mm, normal (0,0.99,0.15), area 283.5mm2, adj f132,f133,f140,f149
  f140: plane 19.62x17.32mm, normal (0.99,0,0.16), area 170.8mm2, adj f2,f7,f133,f134,f137,f139,f141,f146
  f141: plane 15.97x13.46mm, normal (0,-0.99,0.15), area 176.7mm2, adj f134,f140,f142,f146
  f142: plane 19.75x17.62mm, normal (-0.99,0,0.16), area 166mm2, adj f1,f4,f6,f134,f135,f136,f141,f143
  f143: plane 17.31x13.79mm, normal (0,-0.99,0.16), area 109.4mm2, adj f130,f132,f142,f145
  f144: cylinder r=2mm len=13.19mm, axis (0,1,0), area 31.9mm2, adj f0,f111,f142,f145,f146
  f145: cylinder r=2mm len=13.3mm, axis (-1,0,0), area 31.5mm2, adj f0,f132,f143,f144,f147
  f146: cylinder r=2mm len=16.18mm, axis (1,0,0), area 39.5mm2, adj f0,f111,f140,f141,f142,f144,f148
  f147: cylinder r=2mm len=11.11mm, axis (0,1,0), area 18mm2, adj f0,f132,f145,f149
  f148: cylinder r=2mm len=23.46mm, axis (0,1,0), area 59.5mm2, adj f0,f140,f146,f149,f150,f151,f154
  f149: cylinder r=2mm len=28.63mm, axis (-1,0,0), area 74.7mm2, adj f0,f132,f139,f140,f147,f148,f151
  f150: cylinder r=0.4mm len=3.64mm, axis (0,1,0), area 1.2mm2, adj f148,f151,f154
  f151: torus R=2.4mm, axis (-1,0,0), area 0.1mm2, adj f148,f149,f150,f152,f154,f156
  f152: cylinder r=0.4mm len=0.4mm, axis (0,1,0), area 0.1mm2, adj f0,f151,f153,f157
  f153: cylinder r=0.4mm len=4.92mm, axis (-1,0,0), area 1.8mm2, adj f0,f152,f155,f157
  f154: bspline ~5.61x2.56mm, area 5.2mm2, adj f0,f3,f148,f150,f151,f156
  f155: bspline ~8.18x2.59mm, area 9.5mm2, adj f0,f3,f153,f157
  f156: bspline ~1.45x1.39mm, area 0.2mm2, adj f3,f151,f154,f157
  f157: bspline ~5.88x2.65mm, area 2.8mm2, adj f3,f152,f153,f155,f156
  f158: plane 4.88x1.11mm, normal (0.97,0.22,0), area 5mm2, adj f0,f159,f165,f166
  f159: cylinder r=45mm len=1mm, axis (0,0,-1), area 1mm2, adj f0,f158,f160,f166
  f160: plane 5.85x1.34mm, normal (-0.97,-0.22,0), area 6mm2, adj f0,f159,f161,f166
  f161: cylinder r=39mm len=5.93mm, axis (0,0,-1), area 6mm2, adj f0,f160,f162,f166
  f162: plane 5.99x1mm, normal (1,0.07,0), area 6mm2, adj f0,f161,f163,f166
  f163: cylinder r=45mm len=1mm, axis (0,0,-1), area 1mm2, adj f0,f162,f164,f166
  f164: plane 4.98x1mm, normal (-1,-0.09,0), area 5mm2, adj f0,f163,f165,f166
  f165: cylinder r=40mm len=4.22mm, axis (0,0,-1), area 4.3mm2, adj f0,f158,f164,f166
  f166: plane 7.27x6.87mm, normal (0,0,1), area 15.8mm2, adj f158,f159,f160,f161,f162,f163,f164,f165
  f167: plane 1x0.93mm, normal (0.93,0.37,0), area 1mm2, adj f0,f168,f178,f179
  f168: cylinder r=40mm len=2.85mm, axis (0,0,-1), area 3mm2, adj f0,f167,f169,f179
  f169: plane 1.39x1mm, normal (0.93,0.37,0), area 1.5mm2, adj f0,f168,f170,f179
  f170: cylinder r=41.5mm len=2.85mm, axis (0,0,-1), area 3mm2, adj f0,f169,f171,f179
  f171: plane 1x0.93mm, normal (0.93,0.37,0), area 1mm2, adj f0,f170,f172,f179
  f172: cylinder r=42.5mm len=2.85mm, axis (0,0,-1), area 3mm2, adj f0,f171,f173,f179
  f173: plane 1.39x1mm, normal (0.93,0.37,0), area 1.5mm2, adj f0,f172,f174,f179
  f174: cylinder r=44mm len=2.85mm, axis (0,0,-1), area 3mm2, adj f0,f173,f175,f179
  f175: plane 1x0.93mm, normal (0.93,0.37,0), area 1mm2, adj f0,f174,f176,f179
  f176: cylinder r=45mm len=3.78mm, axis (0,0,-1), area 4mm2, adj f0,f175,f177,f179
  f177: plane 5.58x2.22mm, normal (-0.93,-0.37,0), area 6mm2, adj f0,f176,f178,f179
  f178: cylinder r=39mm len=3.79mm, axis (0,0,-1), area 4mm2, adj f0,f167,f177,f179
  f179: plane 6.89x6.01mm, normal (0,0,1), area 15mm2, adj f167,f168,f169,f170,f171,f172,f173,f174
  f180: plane 4.31x2.54mm, normal (0.86,0.51,0), area 5mm2, adj f0,f181,f185,f186
  f181: cylinder r=45mm len=1mm, axis (0,0,-1), area 1mm2, adj f0,f180,f182,f186
  f182: plane 5.17x3.05mm, normal (-0.86,-0.51,0), area 6mm2, adj f0,f181,f183,f186
  f183: cylinder r=39mm len=3.55mm, axis (0,0,-1), area 4mm2, adj f0,f182,f184,f186
  f184: plane 1x0.87mm, normal (0.86,0.51,0), area 1mm2, adj f0,f183,f185,f186
  f185: cylinder r=40mm len=2.68mm, axis (0,0,-1), area 3mm2, adj f0,f180,f184,f186
  f186: plane 6.59x5.67mm, normal (0,0,1), area 9mm2, adj f180,f181,f182,f183,f184,f185
  f187: cylinder r=39mm len=3.22mm, axis (0,0,-1), area 4mm2, adj f0,f188,f198,f199
  f188: plane 1x0.83mm, normal (0.83,0.56,0), area 1mm2, adj f0,f187,f189,f199
  f189: cylinder r=40mm len=2.44mm, axis (0,0,-1), area 3mm2, adj f0,f188,f190,f199
  f190: plane 1.24x1mm, normal (0.83,0.56,0), area 1.5mm2, adj f0,f189,f191,f199
  f191: cylinder r=41.5mm len=2.44mm, axis (0,0,-1), area 3mm2, adj f0,f190,f192,f199
  f192: plane 1x0.83mm, normal (0.83,0.56,0), area 1mm2, adj f0,f191,f193,f199
  f193: cylinder r=42.5mm len=2.44mm, axis (0,0,-1), area 3mm2, adj f0,f192,f194,f199
  f194: plane 1.24x1mm, normal (0.83,0.56,0), area 1.5mm2, adj f0,f193,f195,f199
  f195: cylinder r=44mm len=2.44mm, axis (0,0,-1), area 3mm2, adj f0,f194,f196,f199
  f196: plane 1x0.83mm, normal (0.83,0.57,0), area 1mm2, adj f0,f195,f197,f199
  f197: cylinder r=45mm len=3.23mm, axis (0,0,-1), area 4mm2, adj f0,f196,f198,f199
  f198: plane 4.97x3.4mm, normal (-0.83,-0.56,0), area 6mm2, adj f0,f187,f197,f199
  f199: plane 7.33x6.62mm, normal (0,0,1), area 15mm2, adj f187,f188,f189,f190,f191,f192,f193,f194
  f200: cylinder r=39mm len=2.84mm, axis (0,0,-1), area 4mm2, adj f0,f201,f205,f206
  f201: plane 1x0.71mm, normal (0.71,0.7,0), area 1mm2, adj f0,f200,f202,f206
  f202: cylinder r=40mm len=2.14mm, axis (0,0,-1), area 3mm2, adj f0,f201,f203,f206
  f203: plane 3.77x3.29mm, normal (0.66,0.75,0), area 5mm2, adj f0,f202,f204,f206
  f204: cylinder r=45mm len=1mm, axis (0,0,-1), area 1mm2, adj f0,f203,f205,f206
  f205: plane 4.47x4mm, normal (-0.67,-0.74,0), area 6mm2, adj f0,f200,f204,f206
  f206: plane 7.29x4.74mm, normal (0,0,1), area 9.2mm2, adj f200,f201,f202,f203,f204,f205
  f207: torus R=10mm, axis (0,0,1), area 105mm2, adj f109,f110
PLACE A rot(axis=(0.71,0.71,0),180deg) t=(-46.45,29.94,-13.35)mm
PLACE B rot(axis=(0,0,-1),90deg) t=(-46.84,16.29,4.65)mm
PLACE C rot(axis=(-0.98,-0.04,0.21),0deg) t=(1.05,29.94,-12.85)mm
MATE revolute B.f83 <-> C.f55  axis (0,0,1) through (-46.45,29.94,0.15)mm
MATE planar A.f95 <-> B.f83  axis (0,0,1) through (-46.45,29.94,2.65)mm
